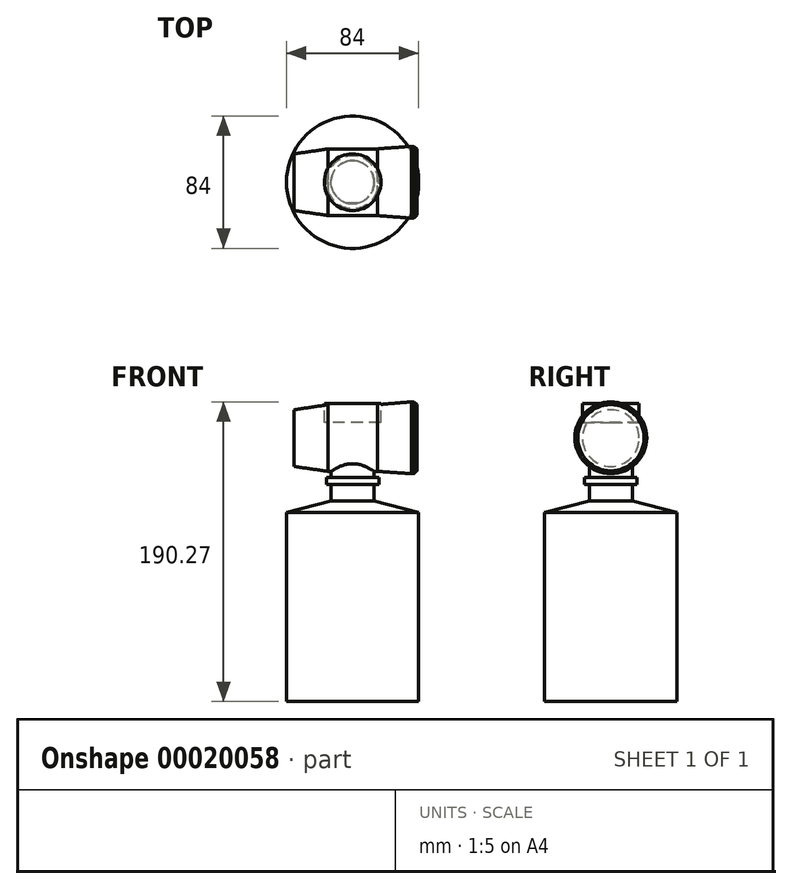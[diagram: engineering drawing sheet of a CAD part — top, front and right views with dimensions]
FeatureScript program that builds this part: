
annotation { "Feature Type Name" : "Feature", "Feature Type Description" : "" }
export const myFeature = defineFeature(function(context is Context, id is Id, definition is map)
    precondition{}
    {
        {
            var Q0;
            Q0=qCreatedBy(makeId("Front.planeOp"),FACE);
            var sketch = newSketch(context, id + "F0", { "sketchPlane" : qUnion([Q0])});
            skLineSegment(sketch, "E0.bottom", {"start": v(0, 0) * mm, "end": v(35, 0) * mm});
            skLineSegment(sketch, "E0.top", {"start": v(0, 100) * mm, "end": v(35, 100) * mm});
            skLineSegment(sketch, "E0.left", {"start": v(0, 0) * mm, "end": v(0, 100) * mm});
            skLineSegment(sketch, "E0.right", {"start": v(35, 0) * mm, "end": v(35, 100) * mm});
            skLineSegment(sketch, "E1", {"start": v(35, 100) * mm, "end": v(0, 109.16) * mm});
            skLineSegment(sketch, "E2", {"start": v(0, 109.16) * mm, "end": v(0, 100) * mm});
            skLineSegment(sketch, "E3.bottom", {"start": v(11.4, 106.17) * mm, "end": v(0, 106.17) * mm});
            skLineSegment(sketch, "E3.top", {"start": v(11.4, 125.65) * mm, "end": v(0, 125.65) * mm});
            skLineSegment(sketch, "E3.left", {"start": v(11.4, 106.17) * mm, "end": v(11.4, 125.65) * mm});
            skLineSegment(sketch, "E3.right", {"start": v(0, 106.17) * mm, "end": v(0, 125.65) * mm});
            skLineSegment(sketch, "E4.bottom", {"start": v(11.4, 118.66) * mm, "end": v(13.83, 118.66) * mm});
            skLineSegment(sketch, "E4.top", {"start": v(11.4, 114.75) * mm, "end": v(13.83, 114.75) * mm});
            skLineSegment(sketch, "E4.left", {"start": v(11.4, 118.66) * mm, "end": v(11.4, 114.75) * mm});
            skLineSegment(sketch, "E4.right", {"start": v(13.83, 118.66) * mm, "end": v(13.83, 114.75) * mm});
            skSolve(sketch);
        }
        {
            var Q0;
            Q0 = qSketchRegion(id + "F0", true);
            var Q1;
            Q1=sQuery(id+"F0.wireOp",EDGE,"E0.left");
            revolve(context, id + "F1", {"entities" : qUnion([Q0]), "axis" : qUnion([Q1]), "revolveType" : RevolveType.FULL});
        }
        {
            var Q0;
            Q0=makeQuery(id+"F1.opRevolve","SWEPT_FACE",FACE,{"disambiguationData":[OSD([sQuery(id+"F0.wireOp",EDGE,"E3.top")])]});
            var sketch = newSketch(context, id + "F2", { "sketchPlane" : qUnion([Q0])});
            skLineSegment(sketch, "E5.rect.bottom", {"start": v(8.1, 8.02) * mm, "end": v(-8.1, 8.02) * mm});
            skLineSegment(sketch, "E5.rect.top", {"start": v(8.1, -8.02) * mm, "end": v(-8.1, -8.02) * mm});
            skLineSegment(sketch, "E5.rect.left", {"start": v(8.1, 8.02) * mm, "end": v(8.1, -8.02) * mm});
            skLineSegment(sketch, "E5.rect.right", {"start": v(-8.1, 8.02) * mm, "end": v(-8.1, -8.02) * mm});
            skPoint(sketch, "E5.rect.middle", {"position": v(0, 0) * mm});
            skSolve(sketch);
        }
        {
            var Q0;
            Q0 = qSketchRegion(id + "F2", true);
            extrude(context, id + "F3", {"entities" : qUnion([Q0]), "operationType" : NewBodyOperationType.ADD, "depth" : 25 * mm});
        }
        {
            var Q0;
            Q0=makeQuery(id+"F3.opExtrude","SWEPT_FACE",FACE,{"disambiguationData":[OSD([sQuery(id+"F2.wireOp",EDGE,"E5.rect.left")])]});
            var sketch = newSketch(context, id + "F4", { "sketchPlane" : qUnion([Q0])});
            skCircle(sketch, "E6", {"center": v(0, 139.4) * mm, "radius": 17.67 * mm});
            skSolve(sketch);
        }
        {
            var Q0;
            Q0 = qSketchRegion(id + "F4", true);
            extrude(context, id + "F5", {"entities" : qUnion([Q0]), "operationType" : NewBodyOperationType.ADD, "depth" : 5 * mm, "hasSecondDirection" : true, "secondDirectionOppositeDirection" : true, "secondDirectionDepth" : 21 * mm});
        }
        {
            var Q0;
            Q0=makeQuery(id+"F5.opExtrude","CAP_FACE",FACE,{"disambiguationData":[OSD([sQuery(id+"F4.wireOp",EDGE,"E6")])],"isStart":false});
            cPlane(context, id + "F6", {"entities" : qUnion([Q0]), "cplaneType" : CPlaneType.OFFSET, "offset" : 18 * mm, "width" : 150 * mm, "height" : 150 * mm});
        }
        {
            var Q0;
            Q0=qCreatedBy(id+"F6.planeOp",FACE);
            var sketch = newSketch(context, id + "F7", { "sketchPlane" : qUnion([Q0])});
            skCircle(sketch, "E7", {"center": v(0, 139.56) * mm, "radius": 19 * mm});
            skSolve(sketch);
        }
        {
            var Q0;
            Q0 = qSketchRegion(id + "F7", true);
            extrude(context, id + "F8", {"entities" : qUnion([Q0]), "depth" : 3 * mm});
        }
        {
            var Q0;
            Q0=makeQuery(id+"F5.opExtrude","CAP_FACE",FACE,{"disambiguationData":[OSD([sQuery(id+"F4.wireOp",EDGE,"E6")])],"isStart":false});
            var Q1;
            Q1=makeQuery(id+"F8.opExtrude","CAP_FACE",FACE,{"disambiguationData":[OSD([sQuery(id+"F7.wireOp",EDGE,"E7")])],"isStart":true});
            loft(context, id + "F9", {"sheetProfilesArray" : [{ "sheetProfileEntities" : qUnion([Q0]) }, { "sheetProfileEntities" : qUnion([Q1]) }]});
        }
        {
            var Q0;
            Q0=makeQuery(id+"F8.opExtrude","CAP_EDGE",EDGE,{"disambiguationData":[OSD([sQuery(id+"F7.wireOp",EDGE,"E7")])],"isStart":false});
            chamfer(context, id + "F10", {"entities" : qUnion([Q0]), "width" : 1.5 * mm, "tangentPropagation" : true});
        }
        {
            var Q0;
            Q0=makeQuery(id+"F5.opExtrude","CAP_FACE",FACE,{"disambiguationData":[OSD([sQuery(id+"F4.wireOp",EDGE,"E6")])],"isStart":true});
            cPlane(context, id + "F11", {"entities" : qUnion([Q0]), "cplaneType" : CPlaneType.OFFSET, "offset" : 18 * mm, "width" : 150 * mm, "height" : 150 * mm});
        }
        {
            var Q0;
            Q0=qCreatedBy(id+"F11.planeOp",FACE);
            var sketch = newSketch(context, id + "F12", { "sketchPlane" : qUnion([Q0])});
            skCircle(sketch, "E8", {"center": v(0, 139.36) * mm, "radius": 15 * mm});
            skSolve(sketch);
        }
        {
            var Q0;
            Q0=makeQuery(id+"F12.imprint","IMPRINT",FACE,{"disambiguationData":[TD([[makeQuery(id+"F12.imprint","IMPRINT",EDGE,{"derivedFrom":sQuery(id+"F12.wireOp",EDGE,"E8")}),1.0]])]});
            var Q1;
            Q1=makeQuery(id+"F5.opExtrude","CAP_FACE",FACE,{"disambiguationData":[OSD([sQuery(id+"F4.wireOp",EDGE,"E6")])],"isStart":true});
            loft(context, id + "F13", {"sheetProfilesArray" : [{ "sheetProfileEntities" : qUnion([Q0]) }, { "sheetProfileEntities" : qUnion([Q1]) }]});
        }
        {
            var Q0;
            Q0=makeQuery(id+"F1.opRevolve","SWEPT_FACE",FACE,{"disambiguationData":[OSD([sQuery(id+"F0.wireOp",EDGE,"E4.bottom")])]});
            cPlane(context, id + "F14", {"entities" : qUnion([Q0]), "cplaneType" : CPlaneType.OFFSET, "offset" : 39 * mm, "width" : 150 * mm, "height" : 150 * mm});
        }
        {
            var Q0;
            Q0=qCreatedBy(id+"F14.planeOp",FACE);
            var sketch = newSketch(context, id + "F15", { "sketchPlane" : qUnion([Q0])});
            skCircle(sketch, "E9", {"center": v(0, 0) * mm, "radius": 15 * mm});
            skSolve(sketch);
        }
        {
            var Q0;
            Q0 = qSketchRegion(id + "F15", true);
            extrude(context, id + "F16", {"entities" : qUnion([Q0]), "oppositeDirection" : true, "depth" : 10 * mm});
        }
        {
            var Q0;
            Q0=makeQuery(id+"F1.opRevolve","SWEPT_BODY",BODY,{"disambiguationData":[OSD([sQuery(id+"F0.wireOp",EDGE,"E0.bottom"),sQuery(id+"F0.wireOp",EDGE,"E0.left"),sQuery(id+"F0.wireOp",EDGE,"E0.right"),sQuery(id+"F0.wireOp",EDGE,"E1"),sQuery(id+"F0.wireOp",EDGE,"E2"),sQuery(id+"F0.wireOp",EDGE,"E3.top"),sQuery(id+"F0.wireOp",EDGE,"E3.left"),sQuery(id+"F0.wireOp",EDGE,"E3.right"),sQuery(id+"F0.wireOp",EDGE,"E4.bottom"),sQuery(id+"F0.wireOp",EDGE,"E4.top"),sQuery(id+"F0.wireOp",EDGE,"E4.right")])]});
            var Q1;
            Q1=makeQuery(id+"F8.opExtrude","SWEPT_BODY",BODY,{"disambiguationData":[OSD([sQuery(id+"F7.wireOp",EDGE,"E7")])]});
            var Q2;
            Q2=makeQuery(id+"F13.opLoft","SWEPT_BODY",BODY,{"disambiguationData":[OSD([sQuery(id+"F4.wireOp",EDGE,"E6"),makeQuery(id+"F12.imprint","IMPRINT",FACE,{"disambiguationData":[TD([[makeQuery(id+"F12.imprint","IMPRINT",EDGE,{"derivedFrom":sQuery(id+"F12.wireOp",EDGE,"E8")}),1.0]])]})])]});
            var Q3;
            Q3=makeQuery(id+"F16.opExtrude","SWEPT_BODY",BODY,{"disambiguationData":[OSD([sQuery(id+"F15.wireOp",EDGE,"E9")])]});
            var Q4;
            Q4=makeQuery(id+"F9.opLoft","SWEPT_BODY",BODY,{"disambiguationData":[OSD([sQuery(id+"F4.wireOp",EDGE,"E6"),sQuery(id+"F7.wireOp",EDGE,"E7")])]});
            var Q5;
            Q5=qCreatedBy(makeId("Origin.pointOp"),VERTEX);
            transform(context, id + "F17", {"entities" : qUnion([Q0, Q1, Q2, Q3, Q4]), "transformType" : TransformType.SCALE_UNIFORMLY, "scale" : 1.2, "makeCopy" : false, "scalePoint" : qUnion([Q5])});
        }
    });
